# Revit family: KLU1_63_UN_Bollard-light_ETK
name_source: partatom
category: Lighting Fixtures
revit_build: Autodesk Revit 2017 (Build: 20190508_0315(x64)
units: mm (PartAtom-declared; Revit-internal decimal feet)

## family parameters
Always vertical = Yes
Cut with Voids When Loaded = No
Light Source = No
OmniClass Number = 23.80.70.11.14.11
OmniClass Title = Downlights
Part Type = Normal
Room Calculation Point = Yes
Round Connector Dimension = Use Diameter
Shared = No
Work Plane-Based = No

## types (16) — shared parameters
Apparent Load = 19 VA
Assembly Code = 63.0
Bundle = 180° - 360°
Description = Bollard light
IfcExportAs = IfcLightFixtureType
IfcExportType = USERDEFINED
Lamp = LED
Luminaire_Body_Material = RAL7024
Manufacturer = ETK licht B.V.
Model = KLU.1
URL = https://www.etk.nl
Voltage = 230 V
Wattage Comments = 19W

## per-type parameters (varying)
| type | Light Source | Luminaire Height |
| KLU.1900 - 19W / 700lm / 3000K | KLU.1 - Lightsource : KLU.1900 - 19W / 700lm / 3000K | 500 mm  [stored 1.64042 ft] |
| KLU.1910 - 19W / 750lm / 4000K | KLU.1 - Lightsource : KLU.1910 - 19W / 750lm / 4000K | 500 mm  [stored 1.64042 ft] |
| KLU.1920 - 19W / 700lm / 3000K | KLU.1 - Lightsource : KLU.1920 - 19W / 700lm / 3000K | 1000 mm  [stored 3.28084 ft] |
| KLU.1930 - 19W / 750lm / 4000K | KLU.1 - Lightsource : KLU.1930 - 19W / 750lm / 4000K | 1000 mm  [stored 3.28084 ft] |
| KLU.1940 - 19W / 1550lm / 3000K | KLU.1 - Lightsource : KLU.1940 - 19W / 1550lm / 3000K | 500 mm  [stored 1.64042 ft] |
| KLU.1950 - 19W / 1650lm / 4000K | KLU.1 - Lightsource : KLU.1950 - 19W / 1650lm / 4000K | 500 mm  [stored 1.64042 ft] |
| KLU.1970 - 19W / 1500lm / 3000K | KLU.1 - Lightsource : KLU.1970 - 19W / 1500lm / 3000K | 1000 mm  [stored 3.28084 ft] |
| KLU.1980 - 19W / 1650lm / 4000K | KLU.1 - Lightsource : KLU.1980 - 19W / 1650lm / 4000K | 1000 mm  [stored 3.28084 ft] |
| KLU.1903 - 19W / 700lm / 3000K | KLU.1 - Lightsource : KLU.1903 - 19W / 700lm / 3000K | 500 mm  [stored 1.64042 ft] |
| KLU.1913 - 19W / 750lm / 4000K | KLU.1 - Lightsource : KLU.1913 - 19W / 750lm / 4000K | 500 mm  [stored 1.64042 ft] |
| KLU.1923 - 19W / 700lm / 3000K | KLU.1 - Lightsource : KLU.1923 - 19W / 700lm / 3000K | 1000 mm  [stored 3.28084 ft] |
| KLU.1933 - 19W / 750lm / 4000K | KLU.1 - Lightsource : KLU.1933 - 19W / 750lm / 4000K | 1000 mm  [stored 3.28084 ft] |
| KLU.1943 - 19W / 1550lm / 3000K | KLU.1 - Lightsource : KLU.1943 - 19W / 1550lm / 3000K | 500 mm  [stored 1.64042 ft] |
| KLU.1953 - 19W / 1650lm / 4000K | KLU.1 - Lightsource : KLU.1900 - 19W / 700lm / 3000K | 500 mm  [stored 1.64042 ft] |
| KLU.1973 - 19W / 1500lm / 3000K | KLU.1 - Lightsource : KLU.1973 - 19W / 1500lm / 3000K | 1000 mm  [stored 3.28084 ft] |
| KLU.1983 - 19W / 1650lm / 4000K | KLU.1 - Lightsource : KLU.1983 - 19W / 1650lm / 4000K | 1000 mm  [stored 3.28084 ft] |

note: [stored X ft] marks values corroborated as IEEE doubles in the binary element streams (Revit-internal decimal feet)

## geometry (parser evidence)
native form markers: Sweep x5
no freeform markers — native parametric forms only
